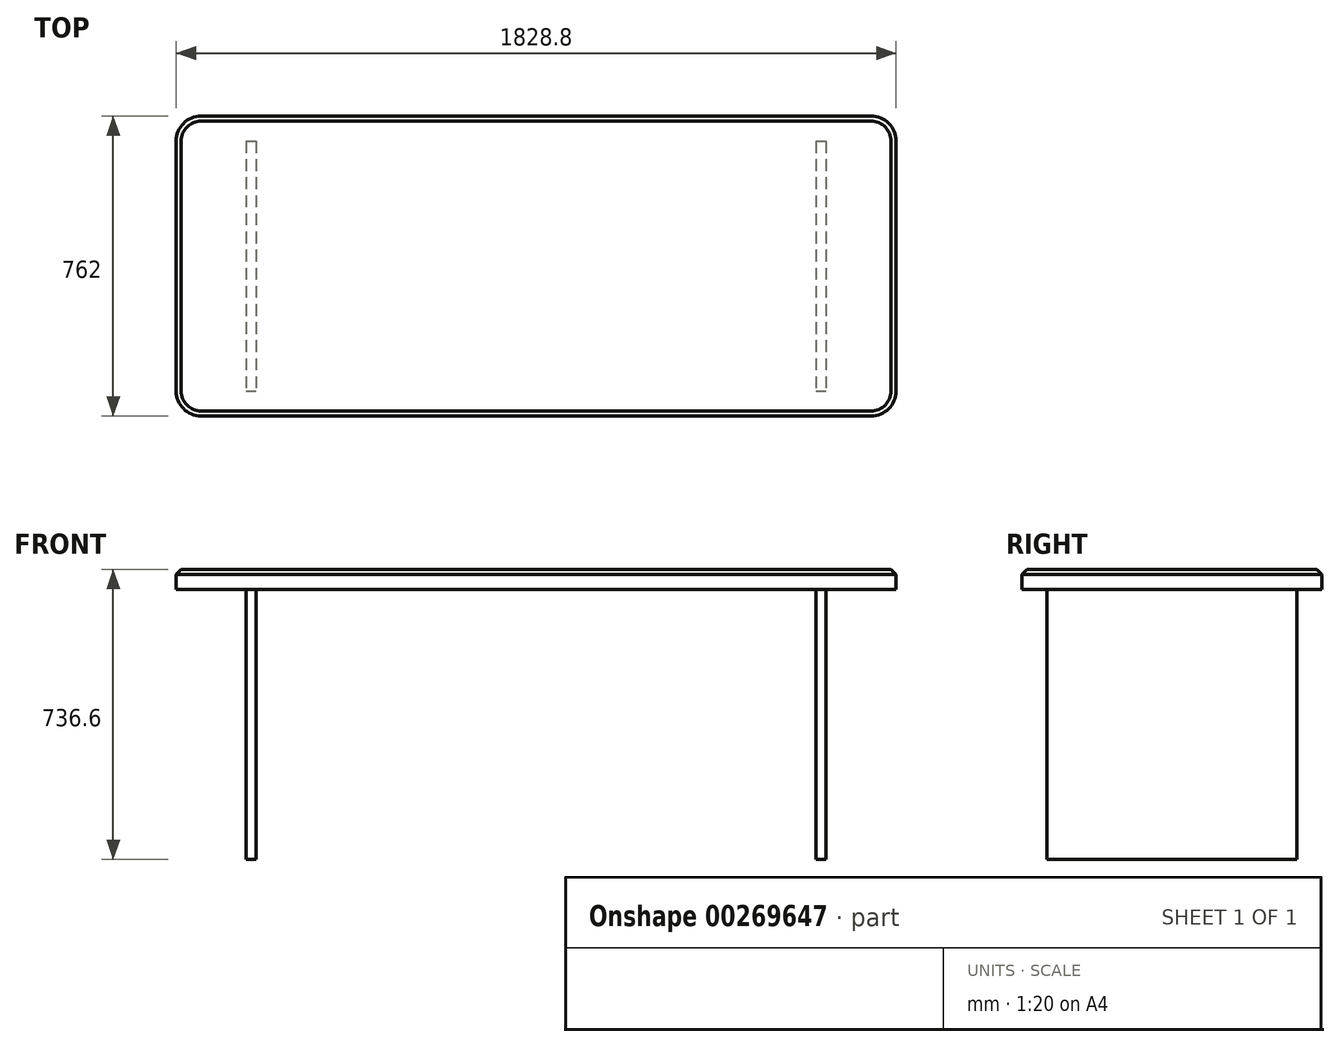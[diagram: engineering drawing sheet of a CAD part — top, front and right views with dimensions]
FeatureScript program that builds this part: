
annotation { "Feature Type Name" : "Feature", "Feature Type Description" : "" }
export const myFeature = defineFeature(function(context is Context, id is Id, definition is map)
    precondition{}
    {
        {
            var Q0;
            Q0=qCreatedBy(makeId("Top.planeOp"),FACE);
            var sketch = newSketch(context, id + "F0", { "sketchPlane" : qUnion([Q0])});
            skLineSegment(sketch, "E0.bottom", {"start": v(63.5, 0) * mm, "end": v(1765.3, 0) * mm});
            skLineSegment(sketch, "E0.top", {"start": v(63.5, 762) * mm, "end": v(1765.3, 762) * mm});
            skLineSegment(sketch, "E0.left", {"start": v(0, 63.5) * mm, "end": v(0, 698.5) * mm});
            skLineSegment(sketch, "E0.right", {"start": v(1828.8, 63.5) * mm, "end": v(1828.8, 698.5) * mm});
            skPoint(sketch, "E1.visualSharp", {"position": v(0, 762) * mm});
            skArc(sketch, "E1.filletArc", {"start": v(63.5, 762) * mm, "mid": v(18.6, 743.4) * mm, "end": v(0, 698.5) * mm});
            skPoint(sketch, "E2.visualSharp", {"position": v(0, 0) * mm});
            skArc(sketch, "E2.filletArc", {"start": v(0, 63.5) * mm, "mid": v(18.6, 18.6) * mm, "end": v(63.5, 0) * mm});
            skPoint(sketch, "E3.visualSharp", {"position": v(1828.8, 0) * mm});
            skArc(sketch, "E3.filletArc", {"start": v(1765.3, 0) * mm, "mid": v(1810.2, 18.6) * mm, "end": v(1828.8, 63.5) * mm});
            skPoint(sketch, "E4.visualSharp", {"position": v(1828.8, 762) * mm});
            skArc(sketch, "E4.filletArc", {"start": v(1828.8, 698.5) * mm, "mid": v(1810.2, 743.4) * mm, "end": v(1765.3, 762) * mm});
            skSolve(sketch);
        }
        {
            var Q0;
            Q0=qCreatedBy(makeId("Top.planeOp"),FACE);
            var sketch = newSketch(context, id + "F1", { "sketchPlane" : qUnion([Q0])});
            skLineSegment(sketch, "E5.bottom", {"start": v(177.8, 698.5) * mm, "end": v(203.2, 698.5) * mm});
            skLineSegment(sketch, "E5.top", {"start": v(177.8, 63.5) * mm, "end": v(203.2, 63.5) * mm});
            skLineSegment(sketch, "E5.left", {"start": v(177.8, 698.5) * mm, "end": v(177.8, 63.5) * mm});
            skLineSegment(sketch, "E5.right", {"start": v(203.2, 698.5) * mm, "end": v(203.2, 63.5) * mm});
            skLineSegment(sketch, "E6.bottom", {"start": v(1625.6, 698.5) * mm, "end": v(1651, 698.5) * mm});
            skLineSegment(sketch, "E6.top", {"start": v(1625.6, 63.5) * mm, "end": v(1651, 63.5) * mm});
            skLineSegment(sketch, "E6.left", {"start": v(1625.6, 698.5) * mm, "end": v(1625.6, 63.5) * mm});
            skLineSegment(sketch, "E6.right", {"start": v(1651, 698.5) * mm, "end": v(1651, 63.5) * mm});
            skSolve(sketch);
        }
        {
            var Q0;
            Q0 = qSketchRegion(id + "F0", true);
            extrude(context, id + "F2", {"entities" : qUnion([Q0]), "depth" : 50.8 * mm});
        }
        {
            var Q0;
            Q0=makeQuery(id+"F2.opExtrude","CAP_EDGE",EDGE,{"disambiguationData":[OSD([sQuery(id+"F0.wireOp",EDGE,"E0.left")])],"isStart":false});
            chamfer(context, id + "F3", {"entities" : qUnion([Q0]), "width" : 12.7 * mm, "tangentPropagation" : true});
        }
        {
            var Q0;
            Q0 = qSketchRegion(id + "F1", true);
            extrude(context, id + "F4", {"entities" : qUnion([Q0]), "operationType" : NewBodyOperationType.ADD, "oppositeDirection" : true, "depth" : 685.8 * mm});
        }
    });
